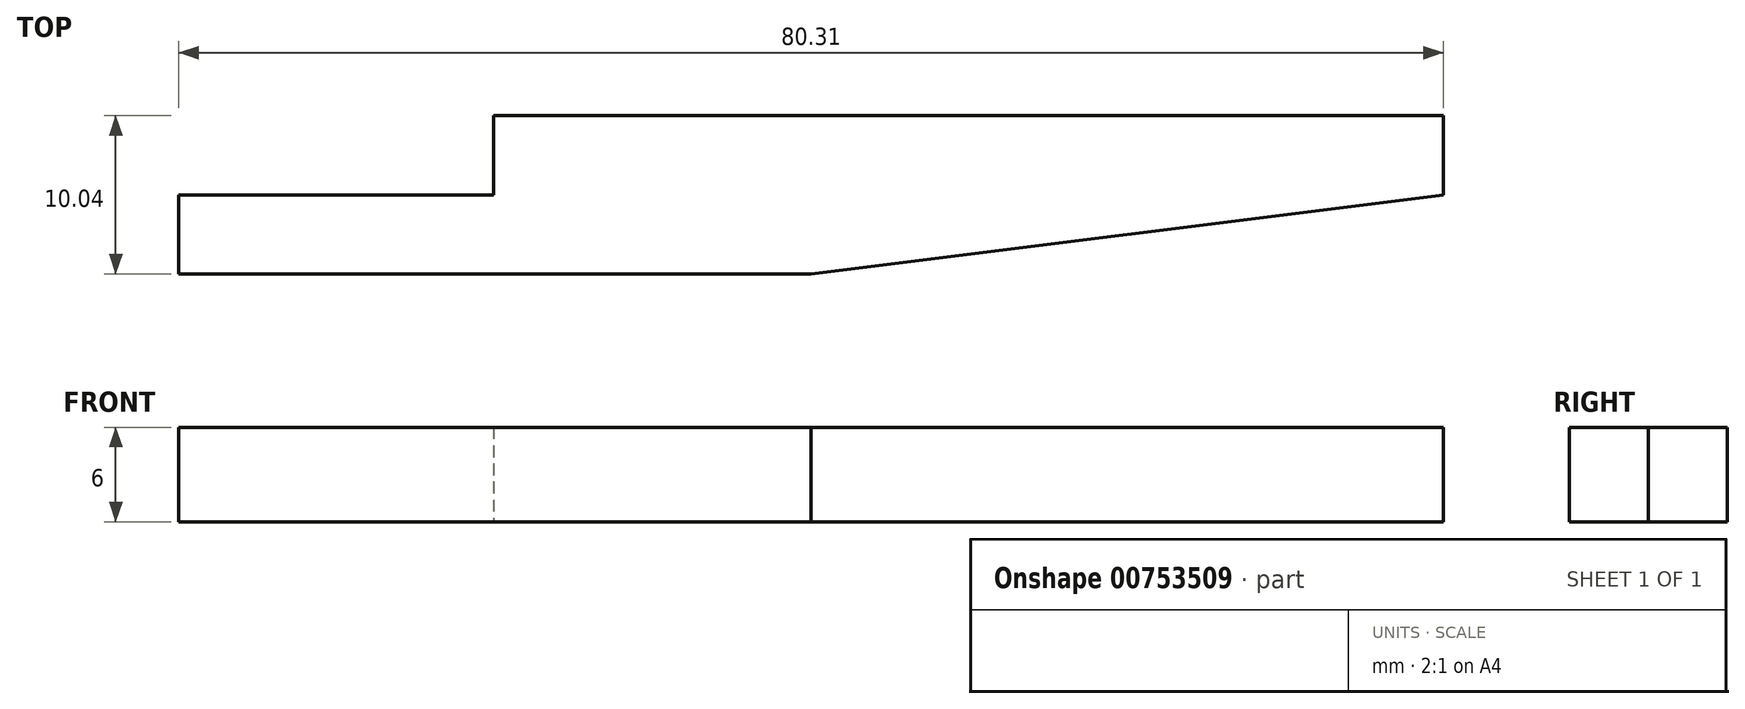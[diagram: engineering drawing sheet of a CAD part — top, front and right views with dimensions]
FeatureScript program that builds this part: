
annotation { "Feature Type Name" : "Feature", "Feature Type Description" : "" }
export const myFeature = defineFeature(function(context is Context, id is Id, definition is map)
    precondition{}
    {
        {
            var Q0;
            Q0=qCreatedBy(makeId("Top.planeOp"),FACE);
            var sketch = newSketch(context, id + "F0", { "sketchPlane" : qUnion([Q0])});
            skLineSegment(sketch, "E0.bottom", {"start": v(-36.56, -11.12) * mm, "end": v(23.75, -11.12) * mm});
            skLineSegment(sketch, "E0.top", {"start": v(-56.56, -21.16) * mm, "end": v(-16.4, -21.16) * mm});
            skLineSegment(sketch, "E0.left", {"start": v(-56.56, -16.14) * mm, "end": v(-56.56, -21.16) * mm});
            skLineSegment(sketch, "E0.right", {"start": v(23.75, -11.12) * mm, "end": v(23.75, -16.14) * mm});
            skLineSegment(sketch, "E1", {"start": v(-56.56, -16.14) * mm, "end": v(-36.56, -16.14) * mm});
            skLineSegment(sketch, "E2", {"start": v(-36.56, -16.14) * mm, "end": v(-36.56, -11.12) * mm});
            skLineSegment(sketch, "E3", {"start": v(23.75, -16.14) * mm, "end": v(-16.4, -21.16) * mm});
            skSolve(sketch);
        }
        {
            var Q0;
            Q0=makeQuery(id+"F0.imprint","IMPRINT",FACE,{"disambiguationData":[TD([[makeQuery(id+"F0.imprint","IMPRINT",EDGE,{"derivedFrom":sQuery(id+"F0.wireOp",EDGE,"E0.bottom")}),-1.0]])]});
            extrude(context, id + "F1", {"entities" : qUnion([Q0]), "depth" : 6 * mm, "offsetDistance" : 25 * mm});
        }
    });
